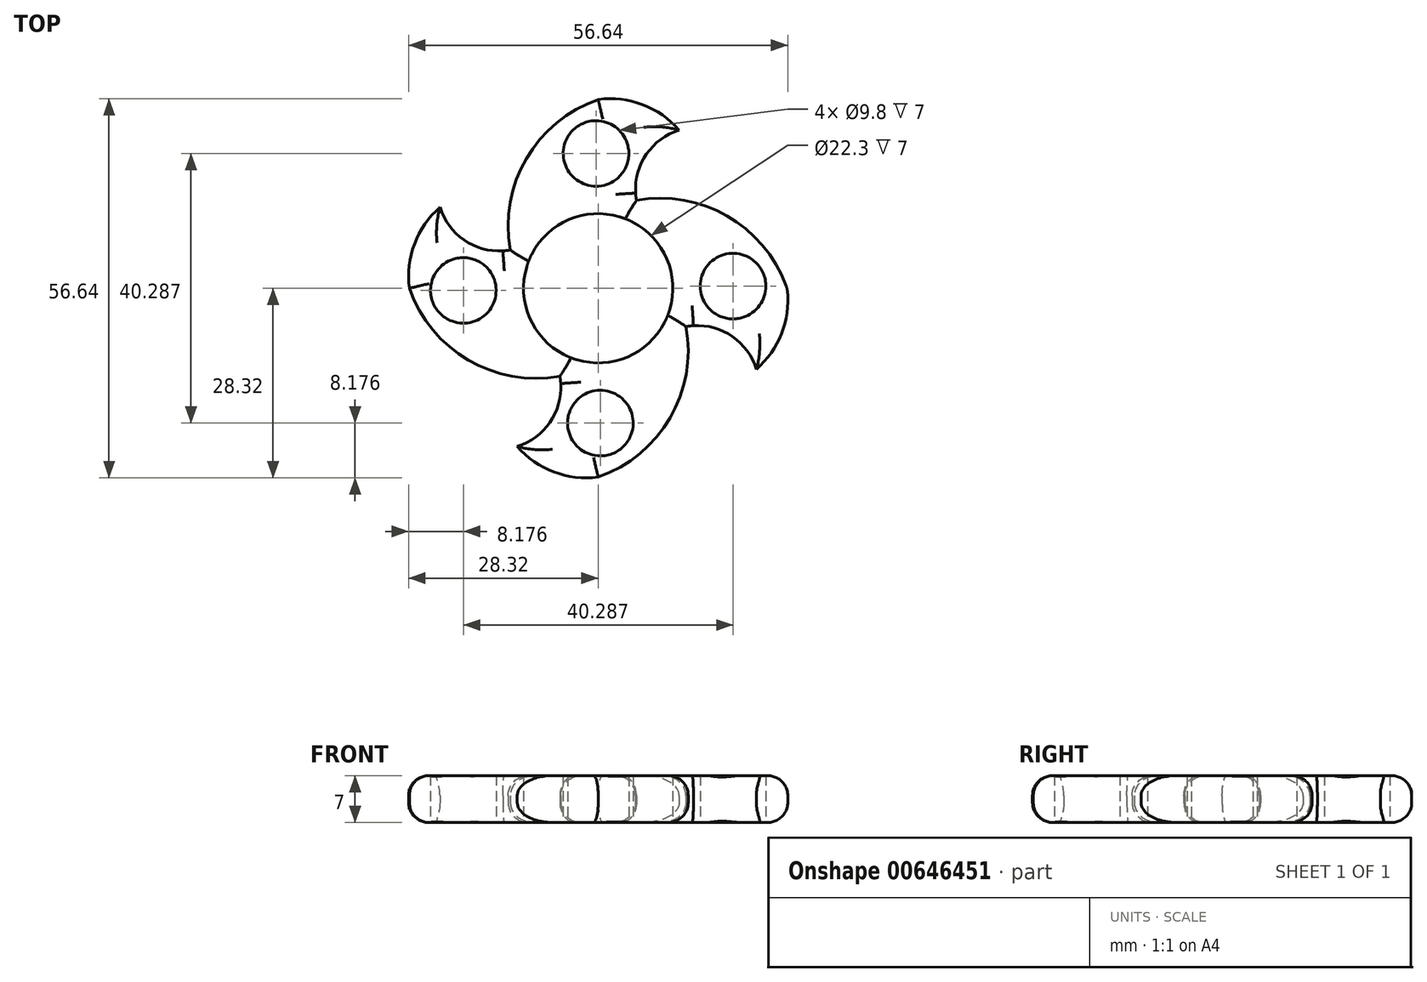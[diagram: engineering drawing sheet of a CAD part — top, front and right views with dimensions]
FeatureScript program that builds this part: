
annotation { "Feature Type Name" : "Feature", "Feature Type Description" : "" }
export const myFeature = defineFeature(function(context is Context, id is Id, definition is map)
    precondition{}
    {
        {
            var Q0;
            Q0=qCreatedBy(makeId("Top.planeOp"),FACE);
            var sketch = newSketch(context, id + "F0", { "sketchPlane" : qUnion([Q0])});
            skCircle(sketch, "E0", {"center": v(0, 0) * mm, "radius": 11.15 * mm});
            skArc(sketch, "E1", {"start": v(23.63, -12.1) * mm, "mid": v(27.44, -6.63) * mm, "end": v(28.2, 0) * mm});
            skArc(sketch, "E2", {"start": v(23.63, -12.1) * mm, "mid": v(20.06, -7.22) * mm, "end": v(14.23, -5.59) * mm});
            skArc(sketch, "E3", {"start": v(14.23, -5.59) * mm, "mid": v(11.06, -6.22) * mm, "end": v(8.15, -7.6) * mm});
            skArc(sketch, "E4", {"start": v(28.2, 0) * mm, "mid": v(16.66, 12.05) * mm, "end": v(0, 11.15) * mm});
            skArc(sketch, "E5.1.0", {"start": v(5.59, 14.23) * mm, "mid": v(6.22, 11.06) * mm, "end": v(7.6, 8.15) * mm});
            skArc(sketch, "E5.1.1", {"start": v(12.1, 23.63) * mm, "mid": v(7.22, 20.06) * mm, "end": v(5.59, 14.23) * mm});
            skArc(sketch, "E5.1.2", {"start": v(12.1, 23.63) * mm, "mid": v(6.63, 27.44) * mm, "end": v(0, 28.2) * mm});
            skArc(sketch, "E5.1.3", {"start": v(0, 28.2) * mm, "mid": v(-12.05, 16.66) * mm, "end": v(-11.15, 0) * mm});
            skArc(sketch, "E5.2.0", {"start": v(-14.23, 5.59) * mm, "mid": v(-11.06, 6.22) * mm, "end": v(-8.15, 7.6) * mm});
            skArc(sketch, "E5.2.1", {"start": v(-23.63, 12.1) * mm, "mid": v(-20.06, 7.22) * mm, "end": v(-14.23, 5.59) * mm});
            skArc(sketch, "E5.2.2", {"start": v(-23.63, 12.1) * mm, "mid": v(-27.44, 6.63) * mm, "end": v(-28.2, 0) * mm});
            skArc(sketch, "E5.2.3", {"start": v(-28.2, 0) * mm, "mid": v(-16.66, -12.05) * mm, "end": v(0, -11.15) * mm});
            skArc(sketch, "E6.1.3.0", {"start": v(-5.59, -14.23) * mm, "mid": v(-6.22, -11.06) * mm, "end": v(-7.6, -8.15) * mm});
            skArc(sketch, "E6.4.3.0", {"start": v(-12.1, -23.63) * mm, "mid": v(-7.22, -20.06) * mm, "end": v(-5.59, -14.23) * mm});
            skArc(sketch, "E6.8.3.0", {"start": v(-12.1, -23.63) * mm, "mid": v(-6.63, -27.44) * mm, "end": v(0, -28.2) * mm});
            skArc(sketch, "E6.12.3.0", {"start": v(0, -28.2) * mm, "mid": v(12.05, -16.66) * mm, "end": v(11.15, 0) * mm});
            skCircle(sketch, "E7", {"center": v(20.14, 0.32) * mm, "radius": 4.9 * mm});
            skCircle(sketch, "E8.1.0", {"center": v(-0.32, 20.14) * mm, "radius": 4.9 * mm});
            skCircle(sketch, "E8.2.0", {"center": v(-20.14, -0.32) * mm, "radius": 4.9 * mm});
            skCircle(sketch, "E8.3.0", {"center": v(0.32, -20.14) * mm, "radius": 4.9 * mm});
            skSolve(sketch);
        }
        {
            var Q0;
            {var subQ0=sQuery(id+"F0.wireOp",EDGE,"E5.1.1");Q0=makeQuery(id+"F0.imprint","IMPRINT",FACE,{"disambiguationData":[TD([[makeQuery(id+"F0.imprint","IMPRINT",EDGE,{"derivedFrom":subQ0}),-1.0]])]});}
            var Q1;
            {var subQ0=sQuery(id+"F0.wireOp",EDGE,"E5.2.1");Q1=makeQuery(id+"F0.imprint","IMPRINT",FACE,{"disambiguationData":[TD([[makeQuery(id+"F0.imprint","IMPRINT",EDGE,{"derivedFrom":subQ0}),-1.0]])]});}
            var Q2;
            {var subQ0=sQuery(id+"F0.wireOp",EDGE,"E5.2.3");var subQ1=sQuery(id+"F0.wireOp",EDGE,"E0");var subQ2=makeQuery(id+"F0.imprint","INTERSECT",VERTEX,{"derivedFrom":[subQ1,subQ0]});Q2=makeQuery(id+"F0.imprint","IMPRINT",FACE,{"disambiguationData":[TD([[makeQuery(id+"F0.imprint","IMPRINT",EDGE,{"disambiguationData":[TD([[subQ2,1.0]])],"derivedFrom":subQ1}),-1.0]])]});}
            var Q3;
            {var subQ0=sQuery(id+"F0.wireOp",EDGE,"E3");var subQ1=sQuery(id+"F0.wireOp",EDGE,"E0");var subQ2=makeQuery(id+"F0.imprint","INTERSECT",VERTEX,{"derivedFrom":[subQ1,subQ0]});Q3=makeQuery(id+"F0.imprint","IMPRINT",FACE,{"disambiguationData":[TD([[makeQuery(id+"F0.imprint","IMPRINT",EDGE,{"disambiguationData":[TD([[subQ2,-1.0]])],"derivedFrom":subQ1}),-1.0]])]});}
            var Q4;
            {var subQ5=sQuery(id+"F0.wireOp",EDGE,"E6.4.3.0");Q4=makeQuery(id+"F0.imprint","IMPRINT",FACE,{"disambiguationData":[TD([[makeQuery(id+"F0.imprint","IMPRINT",EDGE,{"derivedFrom":subQ5}),-1.0]])]});}
            var Q5;
            {var subQ6=sQuery(id+"F0.wireOp",EDGE,"E1");Q5=makeQuery(id+"F0.imprint","IMPRINT",FACE,{"disambiguationData":[TD([[makeQuery(id+"F0.imprint","IMPRINT",EDGE,{"derivedFrom":subQ6}),1.0]])]});}
            var Q6;
            {var subQ0=sQuery(id+"F0.wireOp",EDGE,"E4");var subQ1=sQuery(id+"F0.wireOp",EDGE,"E0");var subQ2=makeQuery(id+"F0.imprint","INTERSECT",VERTEX,{"derivedFrom":[subQ1,subQ0]});Q6=makeQuery(id+"F0.imprint","IMPRINT",FACE,{"disambiguationData":[TD([[makeQuery(id+"F0.imprint","IMPRINT",EDGE,{"disambiguationData":[TD([[subQ2,1.0]])],"derivedFrom":subQ1}),-1.0]])]});}
            var Q7;
            {var subQ0=sQuery(id+"F0.wireOp",EDGE,"E5.1.3");var subQ1=sQuery(id+"F0.wireOp",EDGE,"E0");var subQ2=makeQuery(id+"F0.imprint","INTERSECT",VERTEX,{"derivedFrom":[subQ1,subQ0]});Q7=makeQuery(id+"F0.imprint","IMPRINT",FACE,{"disambiguationData":[TD([[makeQuery(id+"F0.imprint","IMPRINT",EDGE,{"disambiguationData":[TD([[subQ2,1.0]])],"derivedFrom":subQ1}),-1.0]])]});}
            extrude(context, id + "F1", {"entities" : qUnion([Q0, Q1, Q2, Q3, Q4, Q5, Q6, Q7]), "depth" : 7 * mm, "offsetDistance" : 25 * mm});
        }
        {
            var Q0;
            Q0=makeQuery(id+"F1.opExtrude","CAP_EDGE",EDGE,{"disambiguationData":[OSD([sQuery(id+"F0.wireOp",EDGE,"E5.1.1")])],"isStart":false});
            var Q1;
            Q1=makeQuery(id+"F1.opExtrude","CAP_EDGE",EDGE,{"disambiguationData":[OSD([sQuery(id+"F0.wireOp",EDGE,"E5.1.1")])],"isStart":true});
            var Q2;
            Q2=makeQuery(id+"F1.opExtrude","CAP_EDGE",EDGE,{"disambiguationData":[OSD([sQuery(id+"F0.wireOp",EDGE,"E5.1.2")])],"isStart":false});
            var Q3;
            Q3=makeQuery(id+"F1.opExtrude","CAP_EDGE",EDGE,{"disambiguationData":[OSD([sQuery(id+"F0.wireOp",EDGE,"E5.1.3")])],"isStart":false});
            var Q4;
            Q4=makeQuery(id+"F1.opExtrude","CAP_EDGE",EDGE,{"disambiguationData":[OSD([sQuery(id+"F0.wireOp",EDGE,"E5.2.1")])],"isStart":false});
            var Q5;
            Q5=makeQuery(id+"F1.opExtrude","CAP_EDGE",EDGE,{"disambiguationData":[OSD([sQuery(id+"F0.wireOp",EDGE,"E5.2.2")])],"isStart":false});
            var Q6;
            Q6=makeQuery(id+"F1.opExtrude","CAP_EDGE",EDGE,{"disambiguationData":[OSD([sQuery(id+"F0.wireOp",EDGE,"E5.2.3")])],"isStart":false});
            var Q7;
            Q7=makeQuery(id+"F1.opExtrude","CAP_EDGE",EDGE,{"disambiguationData":[OSD([sQuery(id+"F0.wireOp",EDGE,"E6.4.3.0")])],"isStart":false});
            var Q8;
            Q8=makeQuery(id+"F1.opExtrude","CAP_EDGE",EDGE,{"disambiguationData":[OSD([sQuery(id+"F0.wireOp",EDGE,"E6.12.3.0")])],"isStart":true});
            var Q9;
            Q9=makeQuery(id+"F1.opExtrude","CAP_EDGE",EDGE,{"disambiguationData":[OSD([sQuery(id+"F0.wireOp",EDGE,"E2")])],"isStart":false});
            var Q10;
            Q10=makeQuery(id+"F1.opExtrude","CAP_EDGE",EDGE,{"disambiguationData":[OSD([sQuery(id+"F0.wireOp",EDGE,"E1")])],"isStart":false});
            var Q11;
            Q11=makeQuery(id+"F1.opExtrude","CAP_EDGE",EDGE,{"disambiguationData":[OSD([sQuery(id+"F0.wireOp",EDGE,"E4")])],"isStart":true});
            var Q12;
            Q12=makeQuery(id+"F1.opExtrude","CAP_EDGE",EDGE,{"disambiguationData":[OSD([sQuery(id+"F0.wireOp",EDGE,"E3")])],"isStart":false});
            var Q13;
            Q13=makeQuery(id+"F1.opExtrude","CAP_EDGE",EDGE,{"disambiguationData":[OSD([sQuery(id+"F0.wireOp",EDGE,"E6.1.3.0")])],"isStart":false});
            var Q14;
            Q14=makeQuery(id+"F1.opExtrude","CAP_EDGE",EDGE,{"disambiguationData":[OSD([sQuery(id+"F0.wireOp",EDGE,"E5.2.0")])],"isStart":false});
            var Q15;
            Q15=makeQuery(id+"F1.opExtrude","CAP_EDGE",EDGE,{"disambiguationData":[OSD([sQuery(id+"F0.wireOp",EDGE,"E5.1.0")])],"isStart":false});
            var Q16;
            Q16=makeQuery(id+"F1.opExtrude","CAP_EDGE",EDGE,{"disambiguationData":[OSD([sQuery(id+"F0.wireOp",EDGE,"E5.1.3")])],"isStart":true});
            var Q17;
            Q17=makeQuery(id+"F1.opExtrude","CAP_EDGE",EDGE,{"disambiguationData":[OSD([sQuery(id+"F0.wireOp",EDGE,"E5.1.2")])],"isStart":true});
            var Q18;
            Q18=makeQuery(id+"F1.opExtrude","CAP_EDGE",EDGE,{"disambiguationData":[OSD([sQuery(id+"F0.wireOp",EDGE,"E5.2.1")])],"isStart":true});
            var Q19;
            Q19=makeQuery(id+"F1.opExtrude","CAP_EDGE",EDGE,{"disambiguationData":[OSD([sQuery(id+"F0.wireOp",EDGE,"E5.2.0")])],"isStart":true});
            var Q20;
            Q20=makeQuery(id+"F1.opExtrude","CAP_EDGE",EDGE,{"disambiguationData":[OSD([sQuery(id+"F0.wireOp",EDGE,"E5.1.0")])],"isStart":true});
            var Q21;
            Q21=makeQuery(id+"F1.opExtrude","CAP_EDGE",EDGE,{"disambiguationData":[OSD([sQuery(id+"F0.wireOp",EDGE,"E2")])],"isStart":true});
            var Q22;
            Q22=makeQuery(id+"F1.opExtrude","CAP_EDGE",EDGE,{"disambiguationData":[OSD([sQuery(id+"F0.wireOp",EDGE,"E1")])],"isStart":true});
            var Q23;
            Q23=makeQuery(id+"F1.opExtrude","CAP_EDGE",EDGE,{"disambiguationData":[OSD([sQuery(id+"F0.wireOp",EDGE,"E3")])],"isStart":true});
            var Q24;
            Q24=makeQuery(id+"F1.opExtrude","CAP_EDGE",EDGE,{"disambiguationData":[OSD([sQuery(id+"F0.wireOp",EDGE,"E5.2.3")])],"isStart":true});
            var Q25;
            Q25=makeQuery(id+"F1.opExtrude","CAP_EDGE",EDGE,{"disambiguationData":[OSD([sQuery(id+"F0.wireOp",EDGE,"E5.2.2")])],"isStart":true});
            var Q26;
            Q26=makeQuery(id+"F1.opExtrude","CAP_EDGE",EDGE,{"disambiguationData":[OSD([sQuery(id+"F0.wireOp",EDGE,"E6.4.3.0")])],"isStart":true});
            var Q27;
            Q27=makeQuery(id+"F1.opExtrude","CAP_EDGE",EDGE,{"disambiguationData":[OSD([sQuery(id+"F0.wireOp",EDGE,"E6.1.3.0")])],"isStart":true});
            var Q28;
            Q28=makeQuery(id+"F1.opExtrude","CAP_EDGE",EDGE,{"disambiguationData":[OSD([sQuery(id+"F0.wireOp",EDGE,"E6.8.3.0")])],"isStart":true});
            var Q29;
            Q29=makeQuery(id+"F1.opExtrude","CAP_EDGE",EDGE,{"disambiguationData":[OSD([sQuery(id+"F0.wireOp",EDGE,"E4")])],"isStart":false});
            var Q30;
            Q30=makeQuery(id+"F1.opExtrude","CAP_EDGE",EDGE,{"disambiguationData":[OSD([sQuery(id+"F0.wireOp",EDGE,"E6.12.3.0")])],"isStart":false});
            var Q31;
            Q31=makeQuery(id+"F1.opExtrude","SWEPT_EDGE",EDGE,{"disambiguationData":[OSD([sQuery(id+"F0.wireOp",EDGE,"E1"),sQuery(id+"F0.wireOp",EDGE,"E4")])]});
            var Q32;
            Q32=makeQuery(id+"F1.opExtrude","CAP_EDGE",EDGE,{"disambiguationData":[OSD([sQuery(id+"F0.wireOp",EDGE,"E6.8.3.0")])],"isStart":false});
            fillet(context, id + "F2", {"entities" : qUnion([Q0, Q1, Q2, Q3, Q4, Q5, Q6, Q7, Q8, Q9, Q10, Q11, Q12, Q13, Q14, Q15, Q16, Q17, Q18, Q19, Q20, Q21, Q22, Q23, Q24, Q25, Q26, Q27, Q28, Q29, Q30, Q31, Q32]), "radius" : 3 * mm, "tangentPropagation" : true, "allowEdgeOverflow" : false});
        }
    });
